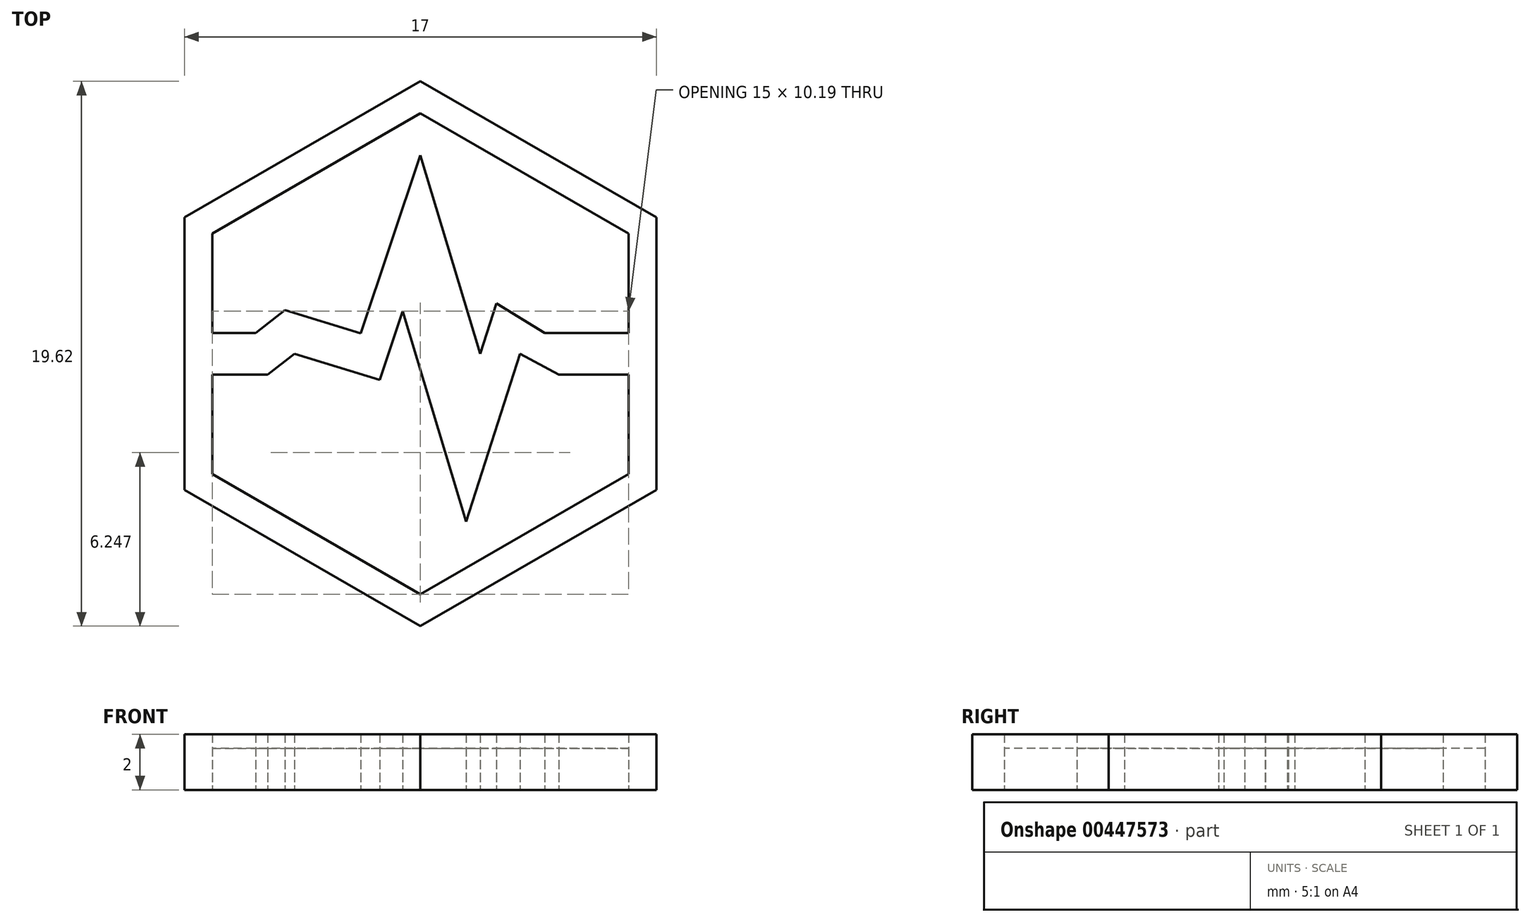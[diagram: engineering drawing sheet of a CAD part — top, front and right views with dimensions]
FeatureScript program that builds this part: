
annotation { "Feature Type Name" : "Feature", "Feature Type Description" : "" }
export const myFeature = defineFeature(function(context is Context, id is Id, definition is map)
    precondition{}
    {
        {
            var Q0;
            Q0=qCreatedBy(makeId("Top.planeOp"),FACE);
            var sketch = newSketch(context, id + "F0", { "sketchPlane" : qUnion([Q0])});
            skCircle(sketch, "E0.cCircle", {"center": v(0, 0) * mm, "radius": 8.5 * mm, "construction": true});
            skLineSegment(sketch, "E0.0", {"start": v(8.5, -4.9) * mm, "end": v(0, -9.81) * mm});
            skLineSegment(sketch, "E0.1", {"start": v(0, -9.81) * mm, "end": v(-8.5, -4.9) * mm});
            skLineSegment(sketch, "E0.2", {"start": v(-8.5, -4.9) * mm, "end": v(-8.5, 4.9) * mm});
            skLineSegment(sketch, "E0.3", {"start": v(-8.5, 4.9) * mm, "end": v(0, 9.81) * mm});
            skLineSegment(sketch, "E0.4", {"start": v(0, 9.81) * mm, "end": v(8.5, 4.9) * mm});
            skLineSegment(sketch, "E0.5", {"start": v(8.5, 4.9) * mm, "end": v(8.5, -4.9) * mm});
            skPoint(sketch, "E0.0.midPoint", {"position": v(4.25, -7.36) * mm});
            skCircle(sketch, "E1.cCircle", {"center": v(0, 0) * mm, "radius": 7.5 * mm, "construction": true});
            skLineSegment(sketch, "E1.0", {"start": v(7.5, -4.33) * mm, "end": v(0, -8.66) * mm});
            skLineSegment(sketch, "E1.1", {"start": v(0, -8.66) * mm, "end": v(-7.5, -4.33) * mm});
            skLineSegment(sketch, "E1.2", {"start": v(-7.5, -4.33) * mm, "end": v(-7.5, -0.75) * mm});
            skLineSegment(sketch, "E1.3", {"start": v(-7.5, 4.33) * mm, "end": v(0, 8.66) * mm});
            skLineSegment(sketch, "E1.4", {"start": v(0, 8.66) * mm, "end": v(7.5, 4.33) * mm});
            skLineSegment(sketch, "E1.5", {"start": v(7.5, 4.33) * mm, "end": v(7.5, 0.75) * mm});
            skPoint(sketch, "E1.0.midPoint", {"position": v(3.75, -6.5) * mm});
            skLineSegment(sketch, "E2", {"start": v(-7.5, 0.75) * mm, "end": v(-5.93, 0.75) * mm});
            skLineSegment(sketch, "E3", {"start": v(-5.93, 0.75) * mm, "end": v(-4.88, 1.57) * mm});
            skLineSegment(sketch, "E4", {"start": v(-4.88, 1.57) * mm, "end": v(-2.15, 0.73) * mm});
            skLineSegment(sketch, "E5", {"start": v(-2.15, 0.73) * mm, "end": v(0, 7.15) * mm});
            skLineSegment(sketch, "E6", {"start": v(0, 7.15) * mm, "end": v(2.15, 0) * mm});
            skLineSegment(sketch, "E7", {"start": v(2.15, 0) * mm, "end": v(2.73, 1.8) * mm});
            skLineSegment(sketch, "E8", {"start": v(2.73, 1.8) * mm, "end": v(4.48, 0.75) * mm});
            skLineSegment(sketch, "E9", {"start": v(4.48, 0.75) * mm, "end": v(7.5, 0.75) * mm});
            skLineSegment(sketch, "E10", {"start": v(-7.5, -0.75) * mm, "end": v(-5.5, -0.75) * mm});
            skLineSegment(sketch, "E11", {"start": v(-5.5, -0.75) * mm, "end": v(-4.54, 0) * mm});
            skLineSegment(sketch, "E12", {"start": v(-4.54, 0) * mm, "end": v(-1.47, -0.94) * mm});
            skLineSegment(sketch, "E13", {"start": v(-1.47, -0.94) * mm, "end": v(-0.64, 1.53) * mm});
            skLineSegment(sketch, "E14", {"start": v(-0.64, 1.53) * mm, "end": v(1.65, -6.05) * mm});
            skLineSegment(sketch, "E15", {"start": v(1.65, -6.05) * mm, "end": v(3.59, 0) * mm});
            skLineSegment(sketch, "E16", {"start": v(3.59, 0) * mm, "end": v(4.98, -0.75) * mm});
            skLineSegment(sketch, "E17", {"start": v(4.98, -0.75) * mm, "end": v(7.5, -0.75) * mm});
            skLineSegment(sketch, "E18.trimOffspring", {"start": v(-7.5, 0.75) * mm, "end": v(-7.5, 4.33) * mm});
            skLineSegment(sketch, "E19.trimOffspring", {"start": v(7.5, -0.75) * mm, "end": v(7.5, -4.33) * mm});
            skSolve(sketch);
        }
        {
            var Q0;
            Q0=makeQuery(id+"F0.imprint","IMPRINT",FACE,{"disambiguationData":[TD([[makeQuery(id+"F0.imprint","IMPRINT",EDGE,{"derivedFrom":sQuery(id+"F0.wireOp",EDGE,"E0.0")}),-1.0]])]});
            extrude(context, id + "F1", {"entities" : qUnion([Q0]), "offsetDistance" : 25 * mm, "depth" : 2 * mm});
        }
        {
            var Q0;
            Q0=makeQuery(id+"F0.imprint","IMPRINT",FACE,{"disambiguationData":[TD([[makeQuery(id+"F0.imprint","IMPRINT",EDGE,{"derivedFrom":sQuery(id+"F0.wireOp",EDGE,"E1.3")}),-1.0]])]});
            var Q1;
            Q1=makeQuery(id+"F0.imprint","IMPRINT",FACE,{"disambiguationData":[TD([[makeQuery(id+"F0.imprint","IMPRINT",EDGE,{"derivedFrom":sQuery(id+"F0.wireOp",EDGE,"E1.0")}),-1.0]])]});
            extrude(context, id + "F2", {"entities" : qUnion([Q0, Q1]), "depth" : 1.5 * mm});
        }
    });
